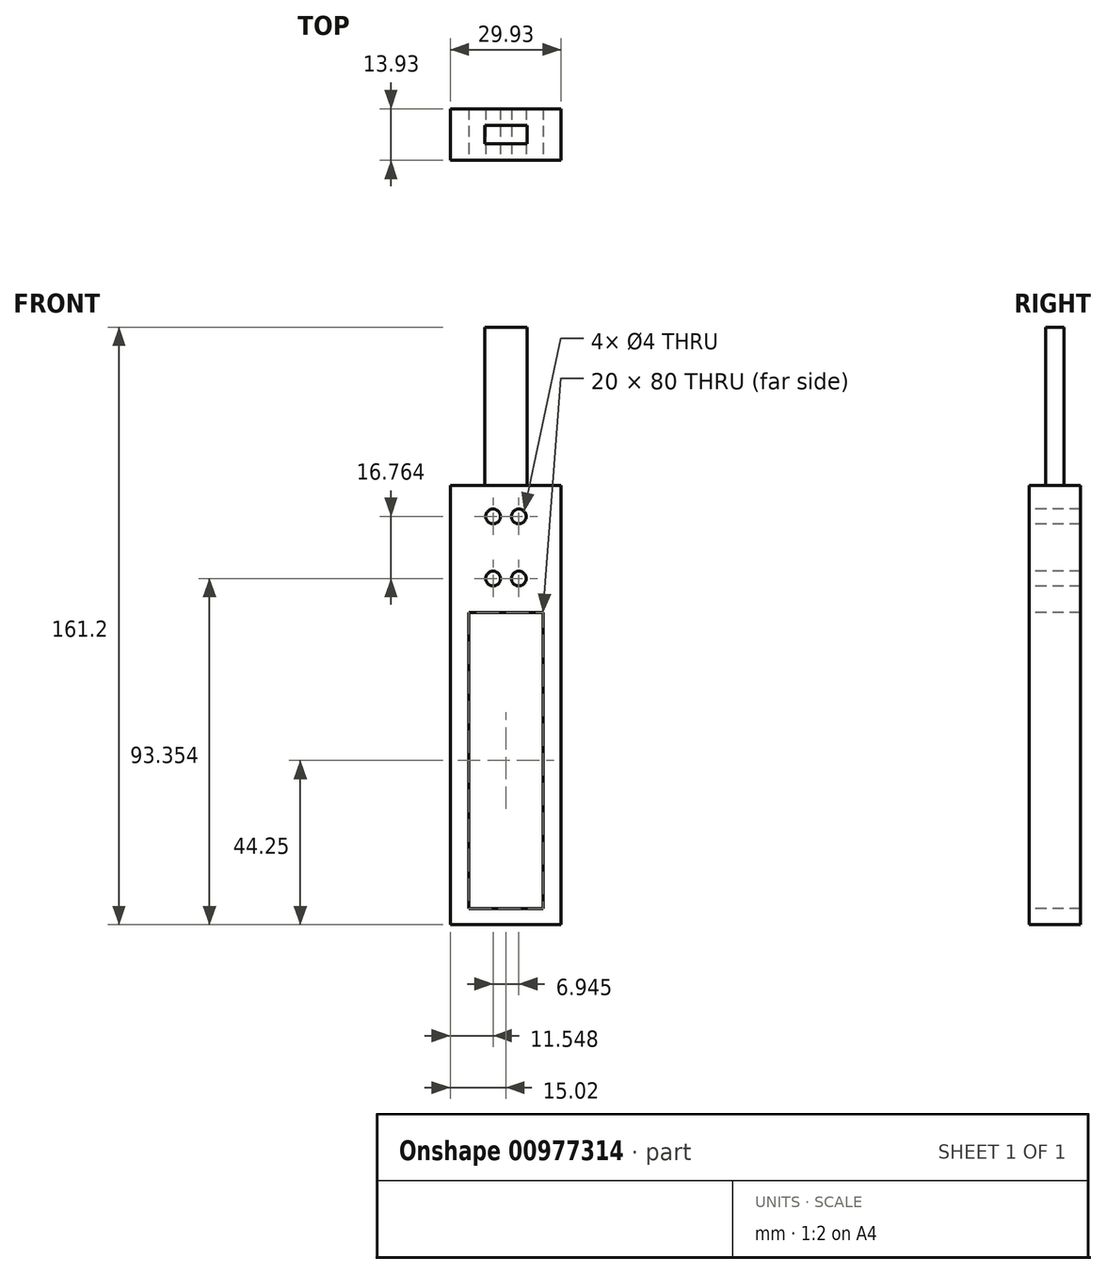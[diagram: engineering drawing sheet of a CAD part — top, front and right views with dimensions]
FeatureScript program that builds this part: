
annotation { "Feature Type Name" : "Feature", "Feature Type Description" : "" }
export const myFeature = defineFeature(function(context is Context, id is Id, definition is map)
    precondition{}
    {
        {
            var Q0;
            Q0=qCreatedBy(makeId("Top.planeOp"),FACE);
            var sketch = newSketch(context, id + "F0", { "sketchPlane" : qUnion([Q0])});
            skCircle(sketch, "E0", {"center": v(0, 0) * mm, "radius": 9.38 * mm});
            skLineSegment(sketch, "E1", {"start": v(14.9, -6.96) * mm, "end": v(14.9, 6.97) * mm});
            skLineSegment(sketch, "E2", {"start": v(-15.02, -6.96) * mm, "end": v(-15.02, 6.97) * mm});
            skLineSegment(sketch, "E3", {"start": v(14.9, -6.96) * mm, "end": v(-15.02, -6.96) * mm});
            skLineSegment(sketch, "E4", {"start": v(14.9, 6.97) * mm, "end": v(-15.02, 6.97) * mm});
            skLineSegment(sketch, "E5.bottom", {"start": v(5.48, 2.92) * mm, "end": v(-5.07, 2.92) * mm});
            skLineSegment(sketch, "E5.top", {"start": v(5.48, -2.92) * mm, "end": v(-5.07, -2.92) * mm});
            skLineSegment(sketch, "E5.left", {"start": v(5.48, 2.92) * mm, "end": v(5.48, -2.92) * mm});
            skLineSegment(sketch, "E5.right", {"start": v(-5.07, 2.92) * mm, "end": v(-5.07, -2.92) * mm});
            skPoint(sketch, "E5.middle", {"position": v(0.2, 0) * mm});
            skSolve(sketch);
        }
        {
            var Q0;
            Q0=makeQuery(id+"F0.imprint","IMPRINT",FACE,{"disambiguationData":[TD([[makeQuery(id+"F0.imprint","IMPRINT",EDGE,{"derivedFrom":sQuery(id+"F0.wireOp",EDGE,"E5.bottom")}),-1.0]])]});
            var Q1;
            {var subQ5=sQuery(id+"F0.wireOp",EDGE,"E1");Q1=makeQuery(id+"F0.imprint","IMPRINT",FACE,{"disambiguationData":[TD([[makeQuery(id+"F0.imprint","IMPRINT",EDGE,{"derivedFrom":subQ5}),1.0]])]});}
            var Q2;
            Q2=makeQuery(id+"F0.imprint","IMPRINT",FACE,{"disambiguationData":[TD([[makeQuery(id+"F0.imprint","IMPRINT",EDGE,{"derivedFrom":sQuery(id+"F0.wireOp",EDGE,"E5.bottom")}),1.0]])]});
            var Q3;
            {var subQ5=sQuery(id+"F0.wireOp",EDGE,"E2");Q3=makeQuery(id+"F0.imprint","IMPRINT",FACE,{"disambiguationData":[TD([[makeQuery(id+"F0.imprint","IMPRINT",EDGE,{"derivedFrom":subQ5}),-1.0]])]});}
            extrude(context, id + "F1", {"entities" : qUnion([Q0, Q1, Q2, Q3]), "depth" : 85 * mm, "offsetDistance" : 25 * mm});
        }
        {
            var Q0;
            Q0=makeQuery(id+"F1.opExtrude","SWEPT_FACE",FACE,{"disambiguationData":[OSD([sQuery(id+"F0.wireOp",EDGE,"E3")])]});
            var sketch = newSketch(context, id + "F2", { "sketchPlane" : qUnion([Q0])});
            skLineSegment(sketch, "E6", {"start": v(0, 0) * mm, "end": v(0, 85) * mm});
            skLineSegment(sketch, "E7", {"start": v(0, 85) * mm, "end": v(14.9, 85) * mm});
            skLineSegment(sketch, "E8", {"start": v(0, 85) * mm, "end": v(-15.02, 85) * mm});
            skPoint(sketch, "E9", {"position": v(0, 51.47) * mm});
            skPoint(sketch, "E10", {"position": v(0, 85) * mm});
            skPoint(sketch, "E11", {"position": v(-6.94, 85) * mm});
            skPoint(sketch, "E12", {"position": v(6.94, 85) * mm});
            skPoint(sketch, "E13", {"position": v(-6.94, 51.47) * mm});
            skPoint(sketch, "E14", {"position": v(6.94, 51.47) * mm});
            skLineSegment(sketch, "E15", {"start": v(-6.94, 85) * mm, "end": v(0, 85) * mm});
            skLineSegment(sketch, "E16", {"start": v(0, 85) * mm, "end": v(6.94, 85) * mm});
            skPoint(sketch, "E17", {"position": v(-3.47, 85) * mm});
            skPoint(sketch, "E18", {"position": v(3.47, 85) * mm});
            skPoint(sketch, "E19", {"position": v(-6.94, 68.24) * mm});
            skPoint(sketch, "E20", {"position": v(6.94, 68.24) * mm});
            skLineSegment(sketch, "E21", {"start": v(-6.94, 68.24) * mm, "end": v(-6.94, 85) * mm});
            skLineSegment(sketch, "E22", {"start": v(6.94, 68.24) * mm, "end": v(6.94, 85) * mm});
            skLineSegment(sketch, "E23", {"start": v(6.94, 68.24) * mm, "end": v(6.94, 51.47) * mm});
            skLineSegment(sketch, "E24", {"start": v(-6.94, 51.47) * mm, "end": v(-6.94, 68.24) * mm});
            skPoint(sketch, "E25", {"position": v(-6.94, 76.62) * mm});
            skPoint(sketch, "E26", {"position": v(6.94, 76.62) * mm});
            skPoint(sketch, "E27", {"position": v(-6.94, 59.85) * mm});
            skPoint(sketch, "E28", {"position": v(6.94, 59.85) * mm});
            skLineSegment(sketch, "E29", {"start": v(0, 51.47) * mm, "end": v(0, 85) * mm});
            skLineSegment(sketch, "E30", {"start": v(-6.94, 59.85) * mm, "end": v(6.94, 59.85) * mm});
            skLineSegment(sketch, "E31", {"start": v(-6.94, 76.62) * mm, "end": v(6.94, 76.62) * mm});
            skPoint(sketch, "E32", {"position": v(0, 59.85) * mm});
            skPoint(sketch, "E33", {"position": v(0, 76.62) * mm});
            skLineSegment(sketch, "E34", {"start": v(0, 59.85) * mm, "end": v(-6.94, 59.85) * mm});
            skLineSegment(sketch, "E35", {"start": v(0, 59.85) * mm, "end": v(6.94, 59.85) * mm});
            skLineSegment(sketch, "E36", {"start": v(-6.94, 76.62) * mm, "end": v(0, 76.62) * mm});
            skLineSegment(sketch, "E37", {"start": v(0, 76.62) * mm, "end": v(6.94, 76.62) * mm});
            skPoint(sketch, "E38", {"position": v(-3.47, 59.85) * mm});
            skPoint(sketch, "E39", {"position": v(3.47, 59.85) * mm});
            skPoint(sketch, "E40", {"position": v(3.47, 76.62) * mm});
            skPoint(sketch, "E41", {"position": v(-3.47, 76.62) * mm});
            skSolve(sketch);
        }
        {
            var Q0;
            Q0=makeQuery(id+"F1.opExtrude","CAP_FACE",FACE,{"disambiguationData":[OSD([sQuery(id+"F0.wireOp",EDGE,"E1"),sQuery(id+"F0.wireOp",EDGE,"E2"),sQuery(id+"F0.wireOp",EDGE,"E3"),sQuery(id+"F0.wireOp",EDGE,"E4")])],"isStart":true});
            extrude(context, id + "F3", {"entities" : qUnion([Q0]), "operationType" : NewBodyOperationType.ADD, "depth" : 33.5 * mm, "offsetDistance" : 25 * mm});
        }
        {
            var Q0;
            Q0=sQuery(id+"F2.wireOp",VERTEX,"E40");
            var Q1;
            Q1=sQuery(id+"F2.wireOp",VERTEX,"E41");
            var Q2;
            Q2=sQuery(id+"F2.wireOp",VERTEX,"E39");
            var Q3;
            Q3=sQuery(id+"F2.wireOp",VERTEX,"E38");
            var Q4;
            Q4=makeQuery(id+"F1.opExtrude","SWEPT_BODY",BODY,{"disambiguationData":[OSD([sQuery(id+"F0.wireOp",EDGE,"E1"),sQuery(id+"F0.wireOp",EDGE,"E2"),sQuery(id+"F0.wireOp",EDGE,"E3"),sQuery(id+"F0.wireOp",EDGE,"E4")])]});
            hole(context, id + "F4", {"style" : HoleStyle.SIMPLE, "endStyle" : HoleEndStyle.THROUGH, "holeDiameter" : 4 * mm, "majorDiameter" : 5 * mm, "isTappedThrough" : true, "tappedDepth" : 12.7 * mm, "tapClearance" : 3, "startFromSketch" : true, "locations" : qUnion([Q0, Q1, Q2, Q3]), "scope" : qUnion([Q4])});
        }
        {
            var Q0;
            Q0=makeQuery(id+"F1.opExtrude","CAP_FACE",FACE,{"disambiguationData":[OSD([sQuery(id+"F0.wireOp",EDGE,"E1"),sQuery(id+"F0.wireOp",EDGE,"E2"),sQuery(id+"F0.wireOp",EDGE,"E3"),sQuery(id+"F0.wireOp",EDGE,"E4")])],"isStart":false});
            var sketch = newSketch(context, id + "F5", { "sketchPlane" : qUnion([Q0])});
            skPoint(sketch, "E42", {"position": v(0, 0) * mm});
            skLineSegment(sketch, "E43.bottom", {"start": v(-5.73, -2.43) * mm, "end": v(5.73, -2.43) * mm});
            skLineSegment(sketch, "E43.top", {"start": v(-5.73, 2.43) * mm, "end": v(5.73, 2.43) * mm});
            skLineSegment(sketch, "E43.left", {"start": v(-5.73, -2.43) * mm, "end": v(-5.73, 2.43) * mm});
            skLineSegment(sketch, "E43.right", {"start": v(5.73, -2.43) * mm, "end": v(5.73, 2.43) * mm});
            skSolve(sketch);
        }
        {
            var Q0;
            Q0=makeQuery(id+"F5.imprint","IMPRINT",FACE,{"disambiguationData":[TD([[makeQuery(id+"F5.imprint","IMPRINT",EDGE,{"derivedFrom":sQuery(id+"F5.wireOp",EDGE,"E43.bottom")}),1.0]])]});
            extrude(context, id + "F6", {"entities" : qUnion([Q0]), "operationType" : NewBodyOperationType.ADD, "depth" : 42.7 * mm, "offsetDistance" : 25 * mm});
        }
        {
            var Q0;
            {var subQ0=sQuery(id+"F0.wireOp",EDGE,"E3");Q0=makeQuery(id+"F3.boolean.opBoolean","MERGE",FACE,{"derivedFrom":[makeQuery(id+"F1.opExtrude","SWEPT_FACE",FACE,{"disambiguationData":[OSD([subQ0])]}),makeQuery(id+"F3.opExtrude","SWEPT_FACE",FACE,{"disambiguationData":[OSD([subQ0])]})]});}
            var sketch = newSketch(context, id + "F7", { "sketchPlane" : qUnion([Q0])});
            skLineSegment(sketch, "E44.bottom", {"start": v(10, 50.75) * mm, "end": v(-10, 50.75) * mm});
            skLineSegment(sketch, "E44.top", {"start": v(10, 0.75) * mm, "end": v(-10, 0.75) * mm});
            skLineSegment(sketch, "E44.left", {"start": v(10, 50.75) * mm, "end": v(10, 0.75) * mm});
            skLineSegment(sketch, "E44.right", {"start": v(-10, 50.75) * mm, "end": v(-10, 0.75) * mm});
            skPoint(sketch, "E44.middle", {"position": v(0, 25.75) * mm});
            skPoint(sketch, "E44.middle.positionSnap0", {"position": v(14.9, 25.75) * mm});
            skPoint(sketch, "E44.centerSnap0", {"position": v(14.9, 25.75) * mm});
            skLineSegment(sketch, "E45.top", {"start": v(10, -29.25) * mm, "end": v(-10, -29.25) * mm});
            skLineSegment(sketch, "E45.left", {"start": v(10, 0.75) * mm, "end": v(10, -29.25) * mm});
            skLineSegment(sketch, "E45.right", {"start": v(-10, 0.75) * mm, "end": v(-10, -29.25) * mm});
            skSolve(sketch);
        }
        {
            var Q0;
            Q0=qSketchRegion(id+"F7",true);
            extrude(context, id + "F8", {"entities" : qUnion([Q0]), "operationType" : NewBodyOperationType.REMOVE, "oppositeDirection" : true, "depth" : 25 * mm, "offsetDistance" : 25 * mm});
        }
    });
